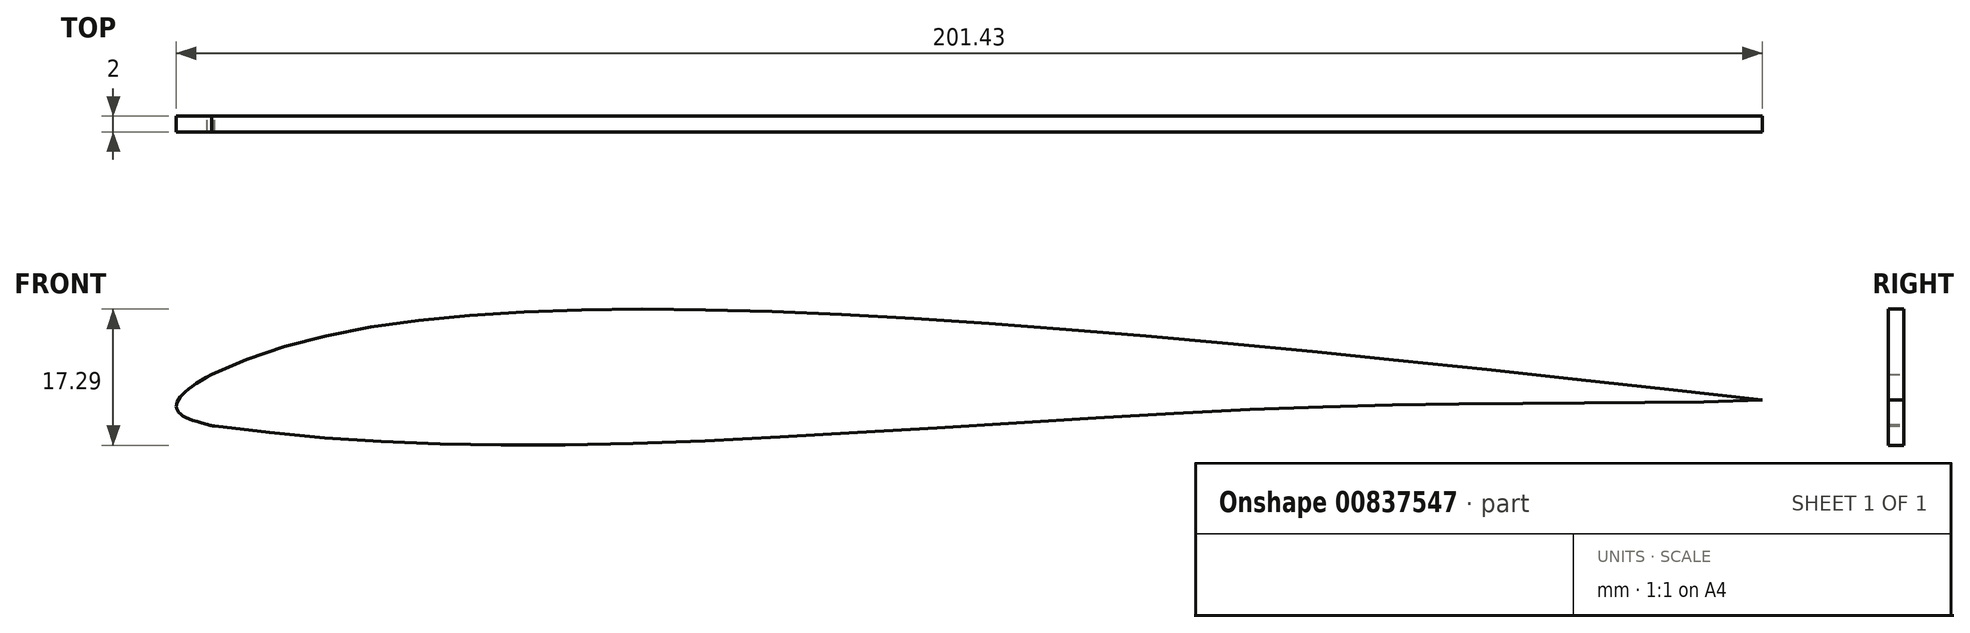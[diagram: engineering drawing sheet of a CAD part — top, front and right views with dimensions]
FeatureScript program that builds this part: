
annotation { "Feature Type Name" : "Feature", "Feature Type Description" : "" }
export const myFeature = defineFeature(function(context is Context, id is Id, definition is map)
    precondition{}
    {
        {
            var Q0;
            Q0=qCreatedBy(makeId("Front.planeOp"),FACE);
            var sketch = newSketch(context, id + "F0", { "sketchPlane" : qUnion([Q0])});
            skPoint(sketch, "E0.middle", {"position": v(0, 0) * mm});
            skLineSegment(sketch, "E1", {"start": v(-100, -4.05) * mm, "end": v(-99.64, -4.05) * mm});
            skFitSpline(sketch, "E2", {"points": [v(-96.98, -0.81) * mm, v(-45.24, 7.5) * mm, v(100, -4.05) * mm], "startDerivative": vector(97.58, 47.67) * mm, "endDerivative": vector(275.05, -31.29) * mm});
            skFitSpline(sketch, "E3", {"points": [v(-96.54, -7.34) * mm, v(-44.56, -9.6) * mm, v(41.7, -4.97) * mm, v(100, -4.05) * mm], "startDerivative": vector(159.07, -20.98) * mm, "endDerivative": vector(169.88, 6) * mm});
            skPoint(sketch, "E4.orphan", {"position": v(-100, 12.5) * mm});
            skPoint(sketch, "E0.right.end.orphan", {"position": v(-100, -12.5) * mm});
            skPoint(sketch, "E5.orphan", {"position": v(100, 12.5) * mm});
            skPoint(sketch, "E0.left.end.orphan", {"position": v(100, -12.5) * mm});
            skFitSpline(sketch, "E6", {"points": [v(-96.54, -7.34) * mm, v(-101.41, -5) * mm, v(-96.98, -0.81) * mm], "startDerivative": vector(-18.7, 3.9) * mm, "endDerivative": vector(17.62, 9.13) * mm});
            skArc(sketch, "E7.trimOffspring", {"start": v(-97.54, -7.12) * mm, "mid": v(-97.05, -7.27) * mm, "end": v(-96.54, -7.34) * mm});
            skSolve(sketch);
        }
        {
            var Q0;
            Q0=qSketchRegion(id+"F0",true);
            extrude(context, id + "F1", {"entities" : qUnion([Q0]), "depth" : 2 * mm, "offsetDistance" : 25 * mm});
        }
    });
